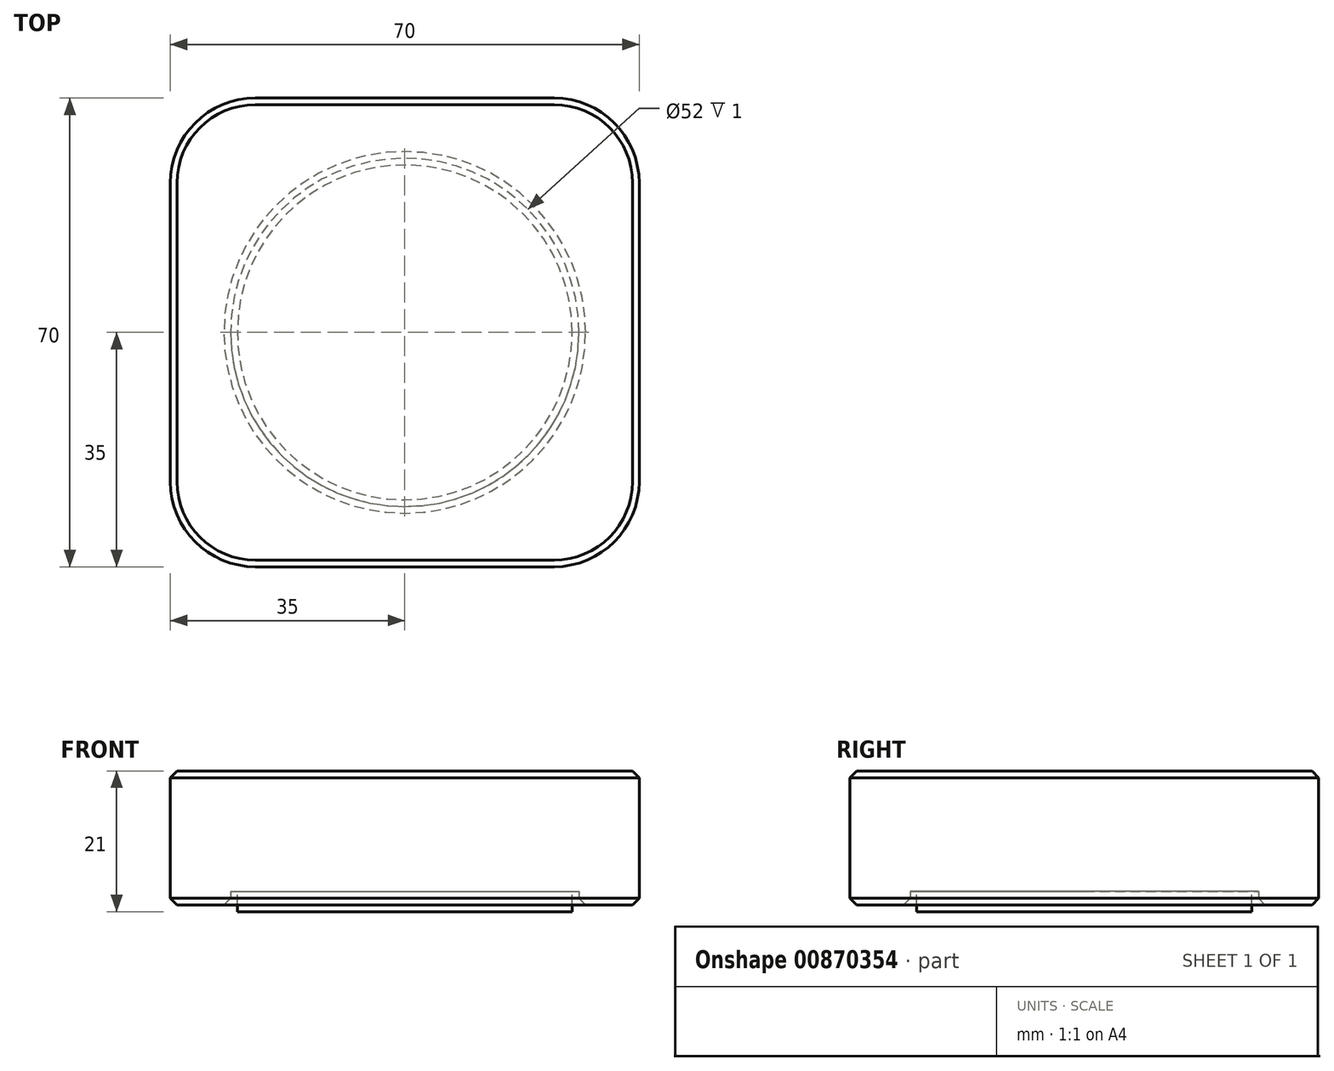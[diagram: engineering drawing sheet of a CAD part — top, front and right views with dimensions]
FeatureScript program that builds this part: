
annotation { "Feature Type Name" : "Feature", "Feature Type Description" : "" }
export const myFeature = defineFeature(function(context is Context, id is Id, definition is map)
    precondition{}
    {
        {
            var Q0;
            Q0=qCreatedBy(makeId("Top.planeOp"),FACE);
            var sketch = newSketch(context, id + "F0", { "sketchPlane" : qUnion([Q0])});
            skLineSegment(sketch, "E0.bottom", {"start": v(35, -35) * mm, "end": v(-35, -35) * mm});
            skLineSegment(sketch, "E0.top", {"start": v(35, 35) * mm, "end": v(-35, 35) * mm});
            skLineSegment(sketch, "E0.left", {"start": v(35, -35) * mm, "end": v(35, 35) * mm});
            skLineSegment(sketch, "E0.right", {"start": v(-35, -35) * mm, "end": v(-35, 35) * mm});
            skPoint(sketch, "E0.middle", {"position": v(0, 0) * mm});
            skSolve(sketch);
        }
        {
            var Q0;
            Q0=makeQuery(id+"F0.imprint","IMPRINT",FACE,{"disambiguationData":[TD([[makeQuery(id+"F0.imprint","IMPRINT",EDGE,{"derivedFrom":sQuery(id+"F0.wireOp",EDGE,"E0.bottom")}),-1.0]])]});
            extrude(context, id + "F1", {"entities" : qUnion([Q0]), "depth" : 20 * mm, "offsetDistance" : 25 * mm});
        }
        {
            var Q0;
            Q0=makeQuery(id+"F1.opExtrude","SWEPT_EDGE",EDGE,{"disambiguationData":[OSD([sQuery(id+"F0.wireOp",EDGE,"E0.bottom"),sQuery(id+"F0.wireOp",EDGE,"E0.left")])]});
            var Q1;
            Q1=makeQuery(id+"F1.opExtrude","SWEPT_EDGE",EDGE,{"disambiguationData":[OSD([sQuery(id+"F0.wireOp",EDGE,"E0.bottom"),sQuery(id+"F0.wireOp",EDGE,"E0.right")])]});
            var Q2;
            Q2=makeQuery(id+"F1.opExtrude","SWEPT_EDGE",EDGE,{"disambiguationData":[OSD([sQuery(id+"F0.wireOp",EDGE,"E0.top"),sQuery(id+"F0.wireOp",EDGE,"E0.left")])]});
            var Q3;
            Q3=makeQuery(id+"F1.opExtrude","SWEPT_EDGE",EDGE,{"disambiguationData":[OSD([sQuery(id+"F0.wireOp",EDGE,"E0.top"),sQuery(id+"F0.wireOp",EDGE,"E0.right")])]});
            fillet(context, id + "F2", {"entities" : qUnion([Q0, Q1, Q2, Q3]), "radius" : 12.7 * mm, "tangentPropagation" : true, "allowEdgeOverflow" : false});
        }
        {
            var Q0;
            Q0=makeQuery(id+"F1.opExtrude","CAP_FACE",FACE,{"disambiguationData":[OSD([sQuery(id+"F0.wireOp",EDGE,"E0.bottom"),sQuery(id+"F0.wireOp",EDGE,"E0.top"),sQuery(id+"F0.wireOp",EDGE,"E0.left"),sQuery(id+"F0.wireOp",EDGE,"E0.right")])],"isStart":true});
            var sketch = newSketch(context, id + "F3", { "sketchPlane" : qUnion([Q0])});
            skCircle(sketch, "E1", {"center": v(0, 0) * mm, "radius": 25 * mm});
            skCircle(sketch, "E2", {"center": v(0, 0) * mm, "radius": 26 * mm});
            skSolve(sketch);
        }
        {
            var Q0;
            Q0=makeQuery(id+"F3.imprint","IMPRINT",FACE,{"disambiguationData":[TD([[makeQuery(id+"F3.imprint","IMPRINT",EDGE,{"derivedFrom":sQuery(id+"F3.wireOp",EDGE,"E1")}),1.0]])]});
            var Q1;
            Q1=makeQuery(id+"F3.imprint","IMPRINT",FACE,{"disambiguationData":[TD([[makeQuery(id+"F3.imprint","IMPRINT",EDGE,{"derivedFrom":sQuery(id+"F3.wireOp",EDGE,"E1")}),-1.0]])]});
            extrude(context, id + "F4", {"entities" : qUnion([Q0, Q1]), "operationType" : NewBodyOperationType.REMOVE, "oppositeDirection" : true, "depth" : 2 * mm, "offsetDistance" : 25 * mm});
        }
        {
            var Q0;
            Q0=makeQuery(id+"F4.boolean.opBoolean","COPY",FACE,{"derivedFrom":makeQuery(id+"F4.opExtrude","CAP_FACE",FACE,{"disambiguationData":[OSD([sQuery(id+"F3.wireOp",EDGE,"E2")])],"isStart":false})});
            var sketch = newSketch(context, id + "F5", { "sketchPlane" : qUnion([Q0])});
            skCircle(sketch, "E3.0", {"center": v(0, 0) * mm, "radius": 25 * mm});
            skSolve(sketch);
        }
        {
            var Q0;
            Q0=makeQuery(id+"F5.imprint","IMPRINT",FACE,{"disambiguationData":[TD([[makeQuery(id+"F5.imprint","IMPRINT",EDGE,{"derivedFrom":sQuery(id+"F5.wireOp",EDGE,"E3.0")}),1.0]])]});
            extrude(context, id + "F6", {"entities" : qUnion([Q0]), "depth" : 3 * mm, "offsetDistance" : 25 * mm});
        }
        {
            var Q0;
            Q0=makeQuery(id+"F1.opExtrude","CAP_FACE",FACE,{"disambiguationData":[OSD([sQuery(id+"F0.wireOp",EDGE,"E0.bottom"),sQuery(id+"F0.wireOp",EDGE,"E0.top"),sQuery(id+"F0.wireOp",EDGE,"E0.left"),sQuery(id+"F0.wireOp",EDGE,"E0.right")])],"isStart":false});
            var Q1;
            Q1=makeQuery(id+"F1.opExtrude","CAP_FACE",FACE,{"disambiguationData":[OSD([sQuery(id+"F0.wireOp",EDGE,"E0.bottom"),sQuery(id+"F0.wireOp",EDGE,"E0.top"),sQuery(id+"F0.wireOp",EDGE,"E0.left"),sQuery(id+"F0.wireOp",EDGE,"E0.right")])],"isStart":true});
            chamfer(context, id + "F7", {"entities" : qUnion([Q0, Q1]), "width" : 1 * mm, "tangentPropagation" : true});
        }
    });
